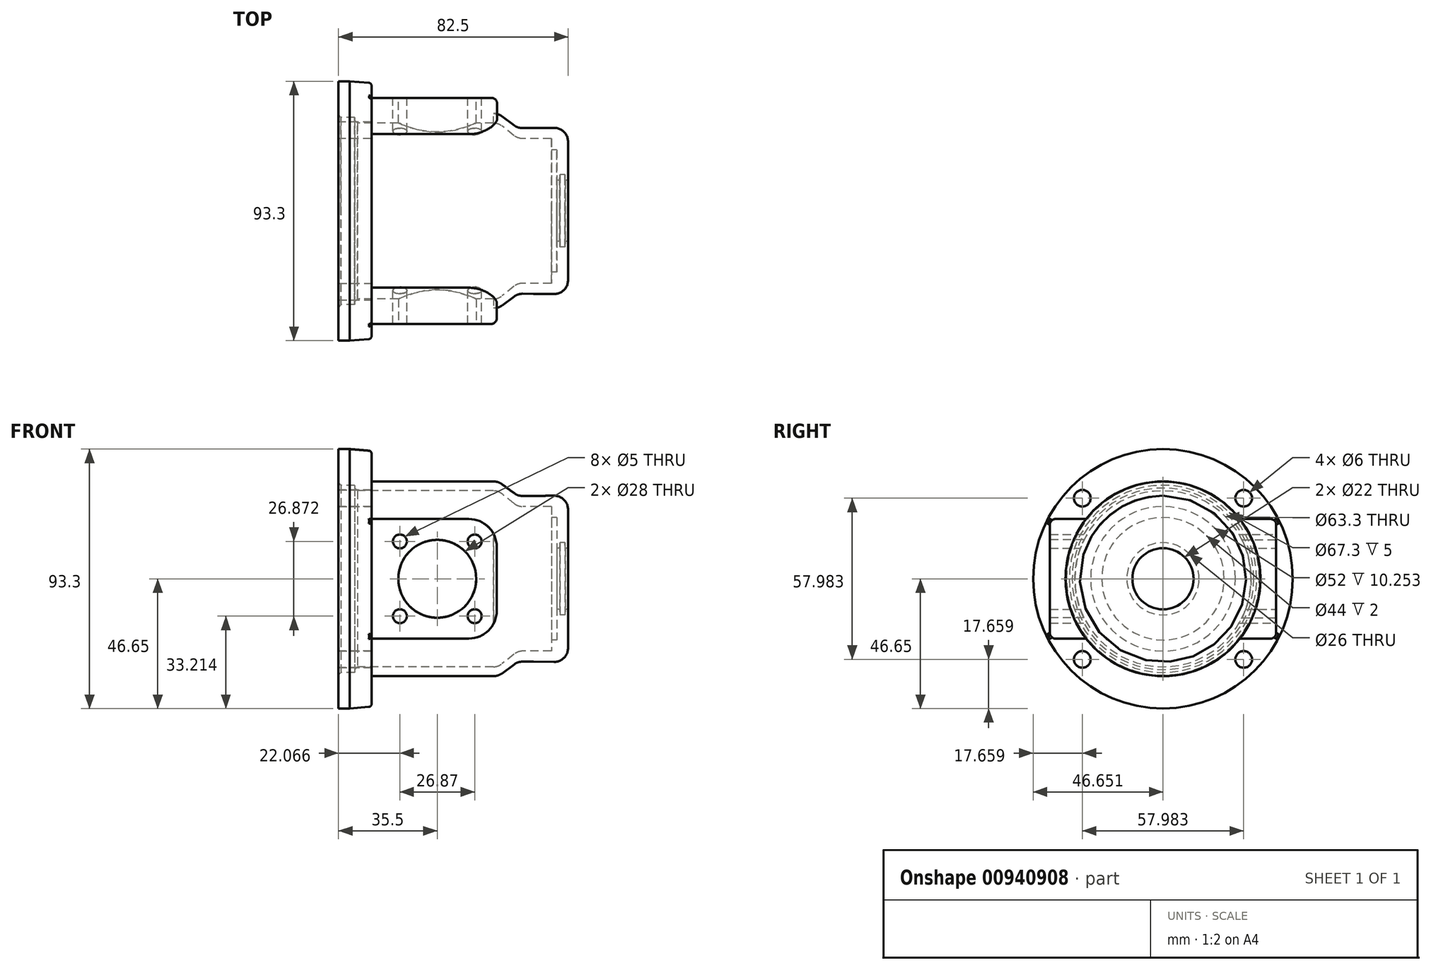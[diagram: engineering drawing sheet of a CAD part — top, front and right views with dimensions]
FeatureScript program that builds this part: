
annotation { "Feature Type Name" : "Feature", "Feature Type Description" : "" }
export const myFeature = defineFeature(function(context is Context, id is Id, definition is map)
    precondition{}
    {
        {
            var Q0;
            Q0=qCreatedBy(makeId("Front.planeOp"),FACE);
            var sketch = newSketch(context, id + "F0", { "sketchPlane" : qUnion([Q0])});
            skLineSegment(sketch, "E0", {"start": v(-19.49, 34.65) * mm, "end": v(-19.49, 46.65) * mm});
            skLineSegment(sketch, "E1", {"start": v(-19.49, 46.65) * mm, "end": v(-15.49, 46.65) * mm});
            skLineSegment(sketch, "E2", {"start": v(-7.63, 46) * mm, "end": v(-15.49, 46.65) * mm});
            skLineSegment(sketch, "E3", {"start": v(-7.63, 46) * mm, "end": v(-7.63, 35) * mm});
            skLineSegment(sketch, "E4", {"start": v(-18.63, 33.65) * mm, "end": v(-19.49, 34.65) * mm});
            skLineSegment(sketch, "E5", {"start": v(-18.63, 33.65) * mm, "end": v(-13.63, 33.65) * mm});
            skLineSegment(sketch, "E6", {"start": v(-13.63, 33.65) * mm, "end": v(-13.63, 32.65) * mm});
            skLineSegment(sketch, "E7", {"start": v(-12.63, 31.65) * mm, "end": v(-13.63, 32.65) * mm});
            skLineSegment(sketch, "E8", {"start": v(0, 0) * mm, "end": v(36.35, 0) * mm});
            skLineSegment(sketch, "E9", {"start": v(57.01, 26) * mm, "end": v(57.01, 22) * mm});
            skPoint(sketch, "E10.newPointB", {"position": v(45.67, 29.78) * mm});
            skPoint(sketch, "E11.orphan", {"position": v(61.56, 0) * mm});
            skLineSegment(sketch, "E12", {"start": v(63.01, 29.93) * mm, "end": v(63.01, 22) * mm});
            skLineSegment(sketch, "E13", {"start": v(13.91, 31.65) * mm, "end": v(33.91, 31.65) * mm});
            skLineSegment(sketch, "E14", {"start": v(-1.09, 35) * mm, "end": v(13.91, 35) * mm});
            skLineSegment(sketch, "E15", {"start": v(-6.09, 31.65) * mm, "end": v(13.91, 31.65) * mm});
            skLineSegment(sketch, "E16", {"start": v(33.91, 31.65) * mm, "end": v(36.17, 31.65) * mm});
            skLineSegment(sketch, "E17", {"start": v(48.77, 26) * mm, "end": v(57.01, 26) * mm});
            skLineSegment(sketch, "E18", {"start": v(50.6, 29.82) * mm, "end": v(63.01, 29.93) * mm});
            skLineSegment(sketch, "E19", {"start": v(-7.63, 35) * mm, "end": v(-1.09, 35) * mm});
            skLineSegment(sketch, "E20", {"start": v(-6.09, 31.65) * mm, "end": v(-12.63, 31.65) * mm});
            skLineSegment(sketch, "E21", {"start": v(46.76, 26) * mm, "end": v(48.77, 26) * mm});
            skLineSegment(sketch, "E22", {"start": v(39.28, 30.56) * mm, "end": v(43.65, 27.09) * mm});
            skPoint(sketch, "E23.visualSharp", {"position": v(37.91, 31.65) * mm});
            skArc(sketch, "E23.filletArc", {"start": v(39.28, 30.56) * mm, "mid": v(37.82, 31.37) * mm, "end": v(36.17, 31.65) * mm});
            skLineSegment(sketch, "E24", {"start": v(50.6, 29.82) * mm, "end": v(46.67, 29.8) * mm});
            skLineSegment(sketch, "E25", {"start": v(43.68, 30.76) * mm, "end": v(39.24, 34.03) * mm});
            skLineSegment(sketch, "E26", {"start": v(13.91, 35) * mm, "end": v(36.28, 35) * mm});
            skPoint(sketch, "E27.visualSharp", {"position": v(37.91, 35) * mm});
            skPoint(sketch, "E28.visualSharp", {"position": v(45.01, 29.78) * mm});
            skArc(sketch, "E28.filletArc", {"start": v(43.68, 30.76) * mm, "mid": v(45.1, 30.04) * mm, "end": v(46.67, 29.8) * mm});
            skArc(sketch, "E29.filletArc", {"start": v(39.24, 34.03) * mm, "mid": v(37.83, 34.75) * mm, "end": v(36.28, 35) * mm});
            skPoint(sketch, "E30.visualSharp", {"position": v(45.01, 26) * mm});
            skArc(sketch, "E30.filletArc", {"start": v(43.65, 27.09) * mm, "mid": v(45.11, 26.28) * mm, "end": v(46.76, 26) * mm});
            skLineSegment(sketch, "E31", {"start": v(63.01, 11) * mm, "end": v(62.51, 11) * mm});
            skLineSegment(sketch, "E32", {"start": v(63.01, 11) * mm, "end": v(63.01, 22) * mm});
            skPoint(sketch, "E33.start.orphan", {"position": v(63.01, 0) * mm});
            skLineSegment(sketch, "E34", {"start": v(57.01, 22) * mm, "end": v(59.01, 22) * mm});
            skLineSegment(sketch, "E35", {"start": v(59.01, 22) * mm, "end": v(59.01, 11) * mm});
            skPoint(sketch, "E36.orphan", {"position": v(57.01, 11) * mm});
            skLineSegment(sketch, "E37", {"start": v(59.01, 11) * mm, "end": v(59.51, 11) * mm});
            skPoint(sketch, "E38.endSnap0", {"position": v(61.01, 11) * mm});
            skLineSegment(sketch, "E39.trimOffspring", {"start": v(59.51, 11) * mm, "end": v(59.01, 11) * mm});
            skLineSegment(sketch, "E40", {"start": v(60.01, 11) * mm, "end": v(59.51, 11) * mm});
            skLineSegment(sketch, "E41", {"start": v(62.01, 11) * mm, "end": v(62.51, 11) * mm});
            skLineSegment(sketch, "E42", {"start": v(60.15, 13) * mm, "end": v(60.01, 11) * mm});
            skLineSegment(sketch, "E43", {"start": v(61.88, 13) * mm, "end": v(62.01, 11) * mm});
            skLineSegment(sketch, "E44", {"start": v(61.01, 11) * mm, "end": v(61.01, 13) * mm});
            skLineSegment(sketch, "E45", {"start": v(61.01, 13) * mm, "end": v(61.88, 13) * mm});
            skLineSegment(sketch, "E46", {"start": v(61.88, 13) * mm, "end": v(60.15, 13) * mm});
            skPoint(sketch, "E47.start.orphan", {"position": v(61.01, 14) * mm});
            skSolve(sketch);
        }
        {
            var Q0;
            Q0=makeQuery(id+"F0.imprint","IMPRINT",FACE,{"disambiguationData":[TD([[makeQuery(id+"F0.imprint","IMPRINT",EDGE,{"derivedFrom":sQuery(id+"F0.wireOp",EDGE,"E0")}),-1.0]])]});
            var Q1;
            Q1=sQuery(id+"F0.wireOp",EDGE,"E8");
            revolve(context, id + "F1", {"surfaceOperationType" : NewSurfaceOperationType.NEW, "entities" : qUnion([Q0]), "axis" : qUnion([Q1]), "revolveType" : RevolveType.FULL});
        }
        {
            var Q0;
            Q0=makeQuery(id+"F1.opRevolve","SWEPT_FACE",FACE,{"disambiguationData":[OSD([sQuery(id+"F0.wireOp",EDGE,"E0")])]});
            var sketch = newSketch(context, id + "F2", { "sketchPlane" : qUnion([Q0])});
            skCircle(sketch, "E48", {"center": v(29, 29) * mm, "radius": 3 * mm});
            skCircle(sketch, "E49", {"center": v(29, -29) * mm, "radius": 3 * mm});
            skCircle(sketch, "E50", {"center": v(-29, 29) * mm, "radius": 3 * mm});
            skCircle(sketch, "E51", {"center": v(-29, -29) * mm, "radius": 3 * mm});
            skSolve(sketch);
        }
        {
            var Q0;
            Q0 = qSketchRegion(id + "F2", true);
            extrude(context, id + "F3", {"entities" : qUnion([Q0]), "operationType" : NewBodyOperationType.REMOVE, "oppositeDirection" : true, "depth" : 18 * mm, "offsetDistance" : 25 * mm});
        }
        {
            var Q0;
            Q0=qCreatedBy(makeId("Front.planeOp"),FACE);
            var sketch = newSketch(context, id + "F4", { "sketchPlane" : qUnion([Q0])});
            skLineSegment(sketch, "E52.bottom", {"start": v(-40.89, 51.65) * mm, "end": v(82.62, 51.65) * mm});
            skLineSegment(sketch, "E52.top", {"start": v(-40.89, -57.32) * mm, "end": v(82.62, -57.32) * mm});
            skLineSegment(sketch, "E52.left", {"start": v(-40.89, 51.65) * mm, "end": v(-40.89, -57.32) * mm});
            skLineSegment(sketch, "E52.right", {"start": v(82.62, 51.65) * mm, "end": v(82.62, -57.32) * mm});
            skSolve(sketch);
        }
        {
            var Q0;
            Q0 = qSketchRegion(id + "F4", true);
            extrude(context, id + "F5", {"entities" : qUnion([Q0]), "operationType" : NewBodyOperationType.REMOVE, "depth" : 50 * mm, "offsetDistance" : 25 * mm});
        }
        {
            var Q0;
            Q0=makeQuery(id+"F1.opRevolve","SWEPT_FACE",FACE,{"disambiguationData":[OSD([sQuery(id+"F0.wireOp",EDGE,"E3")])]});
            var sketch = newSketch(context, id + "F6", { "sketchPlane" : qUnion([Q0])});
            skLineSegment(sketch, "E53", {"start": v(27.62, 21.5) * mm, "end": v(40.67, 21.5) * mm});
            skLineSegment(sketch, "E54", {"start": v(40.67, -21.5) * mm, "end": v(27.62, -21.5) * mm});
            skArc(sketch, "E55", {"start": v(27.62, -21.5) * mm, "mid": v(35, 0) * mm, "end": v(27.62, 21.5) * mm});
            skLineSegment(sketch, "E56", {"start": v(40.67, -21.5) * mm, "end": v(40.67, 21.5) * mm});
            skSolve(sketch);
        }
        {
            var Q0;
            Q0 = qSketchRegion(id + "F6", true);
            extrude(context, id + "F7", {"entities" : qUnion([Q0]), "operationType" : NewBodyOperationType.ADD, "depth" : 45.14 * mm, "offsetDistance" : 25 * mm});
        }
        {
            var Q0;
            Q0=makeQuery(id+"F1.opRevolve","SWEPT_EDGE",EDGE,{"disambiguationData":[OSD([sQuery(id+"F0.wireOp",EDGE,"E0"),sQuery(id+"F0.wireOp",EDGE,"E1")])]});
            cPoint(context, id + "F8", {"entities" : qUnion([Q0]), "parameter" : 0.5});
        }
        {
            var Q0;
            Q0=makeQuery(id+"F1.opRevolve","SWEPT_BODY",BODY,{"disambiguationData":[OSD([sQuery(id+"F0.wireOp",EDGE,"E0"),sQuery(id+"F0.wireOp",EDGE,"E1"),sQuery(id+"F0.wireOp",EDGE,"E2"),sQuery(id+"F0.wireOp",EDGE,"E3"),sQuery(id+"F0.wireOp",EDGE,"E4"),sQuery(id+"F0.wireOp",EDGE,"E5"),sQuery(id+"F0.wireOp",EDGE,"E6"),sQuery(id+"F0.wireOp",EDGE,"E7"),sQuery(id+"F0.wireOp",EDGE,"E9"),sQuery(id+"F0.wireOp",EDGE,"ttlMiW8K-Gj9s-mpOc-sAAF-bqFsmYQRB0dC"),sQuery(id+"F0.wireOp",EDGE,"dxv8NDji-zJk3-8ekn-KFhB-3ztd8SCryWd5"),sQuery(id+"F0.wireOp",EDGE,"E10.filletArc"),sQuery(id+"F0.wireOp",EDGE,"ruUsSjiC-r07a-THA8-P1NI-kNvXG15OnYoc"),sQuery(id+"F0.wireOp",EDGE,"abe5eb92-0ac8-4b74-8677-3c686329f105.filletArc"),sQuery(id+"F0.wireOp",EDGE,"h7bsjftr-fzGa-4ARr-nZfh-VTAOwtfqHb7T"),sQuery(id+"F0.wireOp",EDGE,"3mzqurQ0-g41q-c2LK-6E9X-WYiRKidhnamJ"),sQuery(id+"F0.wireOp",EDGE,"E12"),sQuery(id+"F0.wireOp",EDGE,"bZ8bIDva-nSo4-pdI0-vQef-kBVdg5MjayZi"),sQuery(id+"F0.wireOp",EDGE,"E13"),sQuery(id+"F0.wireOp",EDGE,"sj1dmuSO-go3f-yCpV-ps0s-w3yi9DrHe0LX"),sQuery(id+"F0.wireOp",EDGE,"h7XH48Ex-fpgu-Afb6-qUXn-9KPbAsaJLCzl")])]});
            var Q1;
            Q1 = qCreatedBy(id + "F8" ,VERTEX);
            var Q2;
            Q2=qCreatedBy(makeId("Origin.pointOp"),VERTEX);
            transform(context, id + "F9", {"entities" : qUnion([Q0]), "transformType" : TransformType.TRANSLATION_ENTITY, "oppositeDirectionEntity" : false, "transformLine" : qUnion([Q1, Q2]), "makeCopy" : false});
        }
        {
            var Q0;
            Q0=qCreatedBy(makeId("Front.planeOp"),FACE);
            var sketch = newSketch(context, id + "F10", { "sketchPlane" : qUnion([Q0])});
            skCircle(sketch, "E57", {"center": v(35.5, 0) * mm, "radius": 14 * mm});
            skSolve(sketch);
        }
        {
            var Q0;
            Q0 = qSketchRegion(id + "F10", true);
            extrude(context, id + "F11", {"entities" : qUnion([Q0]), "operationType" : NewBodyOperationType.REMOVE, "depth" : 25 * mm, "offsetDistance" : 25 * mm});
        }
        {
            var Q0;
            Q0=makeQuery(id+"F7.opExtrude","CAP_EDGE",EDGE,{"disambiguationData":[OSD([sQuery(id+"F6.wireOp",EDGE,"E54")])],"isStart":false});
            var Q1;
            Q1=makeQuery(id+"F7.opExtrude","CAP_EDGE",EDGE,{"disambiguationData":[OSD([sQuery(id+"F6.wireOp",EDGE,"E53")])],"isStart":false});
            fillet(context, id + "F12", {"entities" : qUnion([Q0, Q1]), "radius" : 10 * mm, "tangentPropagation" : true, "allowEdgeOverflow" : false});
        }
        {
            var Q0;
            Q0=makeQuery(id+"F7.opExtrude","SWEPT_EDGE",EDGE,{"disambiguationData":[OSD([sQuery(id+"F0.wireOp",EDGE,"E2"),sQuery(id+"F0.wireOp",EDGE,"E3"),sQuery(id+"F6.wireOp",EDGE,"E53"),sQuery(id+"F6.wireOp",EDGE,"E56")])]});
            fillet(context, id + "F13", {"entities" : qUnion([Q0]), "radius" : 2 * mm, "tangentPropagation" : true, "allowEdgeOverflow" : false});
        }
        {
            var Q0;
            Q0=makeQuery(id+"F1.opRevolve","SWEPT_EDGE",EDGE,{"disambiguationData":[OSD([sQuery(id+"F0.wireOp",EDGE,"E12"),sQuery(id+"F0.wireOp",EDGE,"E18")])]});
            fillet(context, id + "F14", {"entities" : qUnion([Q0]), "radius" : 5 * mm, "tangentPropagation" : true, "allowEdgeOverflow" : false});
        }
        {
            var Q0;
            {var subQ0=sQuery(id+"F0.wireOp",EDGE,"E3");var subQ1=sQuery(id+"F0.wireOp",EDGE,"E2");Q0=makeQuery(id+"F7.boolean.opBoolean","SPLIT",EDGE,{"disambiguationData":[TD([makeQuery(id+"F1.opRevolve","SWEPT_FACE",FACE,{"disambiguationData":[OSD([subQ1])]}),makeQuery(id+"F1.opRevolve","SWEPT_FACE",FACE,{"disambiguationData":[OSD([subQ0])]}),makeQuery(id+"F5.boolean.opBoolean","COPY",FACE,{"disambiguationData":[OD(0.0)],"derivedFrom":makeQuery(id+"F5.opExtrude","CAP_FACE",FACE,{"disambiguationData":[OSD([sQuery(id+"F4.wireOp",EDGE,"E52.bottom"),sQuery(id+"F4.wireOp",EDGE,"E52.top"),sQuery(id+"F4.wireOp",EDGE,"E52.left"),sQuery(id+"F4.wireOp",EDGE,"E52.right")])],"isStart":true})}),makeQuery(id+"F7.opExtrude","SWEPT_FACE",FACE,{"disambiguationData":[OSD([sQuery(id+"F6.wireOp",EDGE,"E54")])]}),makeQuery(id+"F7.opExtrude","SWEPT_FACE",FACE,{"disambiguationData":[OSD([sQuery(id+"F6.wireOp",EDGE,"E56")])]})])],"derivedFrom":makeQuery(id+"F1.opRevolve","SWEPT_EDGE",EDGE,{"disambiguationData":[OSD([subQ1,subQ0])]})});}
            var Q1;
            {var subQ0=sQuery(id+"F0.wireOp",EDGE,"E3");var subQ1=sQuery(id+"F0.wireOp",EDGE,"E2");Q1=makeQuery(id+"F7.boolean.opBoolean","SPLIT",EDGE,{"disambiguationData":[TD([makeQuery(id+"F1.opRevolve","SWEPT_FACE",FACE,{"disambiguationData":[OSD([subQ1])]}),makeQuery(id+"F1.opRevolve","SWEPT_FACE",FACE,{"disambiguationData":[OSD([subQ0])]}),makeQuery(id+"F7.opExtrude","SWEPT_FACE",FACE,{"disambiguationData":[OSD([sQuery(id+"F6.wireOp",EDGE,"E53")])]}),makeQuery(id+"F7.opExtrude","SWEPT_FACE",FACE,{"disambiguationData":[OSD([sQuery(id+"F6.wireOp",EDGE,"E54")])]}),makeQuery(id+"F7.opExtrude","SWEPT_FACE",FACE,{"disambiguationData":[OSD([sQuery(id+"F6.wireOp",EDGE,"E56")])]})])],"derivedFrom":makeQuery(id+"F1.opRevolve","SWEPT_EDGE",EDGE,{"disambiguationData":[OSD([subQ1,subQ0])]})});}
            var Q2;
            {var subQ0=sQuery(id+"F0.wireOp",EDGE,"E3");var subQ1=sQuery(id+"F0.wireOp",EDGE,"E2");Q2=makeQuery(id+"F7.boolean.opBoolean","SPLIT",EDGE,{"disambiguationData":[TD([makeQuery(id+"F1.opRevolve","SWEPT_FACE",FACE,{"disambiguationData":[OSD([subQ1])]}),makeQuery(id+"F1.opRevolve","SWEPT_FACE",FACE,{"disambiguationData":[OSD([subQ0])]}),makeQuery(id+"F5.boolean.opBoolean","COPY",FACE,{"disambiguationData":[OD(1.0)],"derivedFrom":makeQuery(id+"F5.opExtrude","CAP_FACE",FACE,{"disambiguationData":[OSD([sQuery(id+"F4.wireOp",EDGE,"E52.bottom"),sQuery(id+"F4.wireOp",EDGE,"E52.top"),sQuery(id+"F4.wireOp",EDGE,"E52.left"),sQuery(id+"F4.wireOp",EDGE,"E52.right")])],"isStart":true})}),makeQuery(id+"F7.opExtrude","SWEPT_FACE",FACE,{"disambiguationData":[OSD([sQuery(id+"F6.wireOp",EDGE,"E53")])]}),makeQuery(id+"F7.opExtrude","SWEPT_FACE",FACE,{"disambiguationData":[OSD([sQuery(id+"F6.wireOp",EDGE,"E56")])]})])],"derivedFrom":makeQuery(id+"F1.opRevolve","SWEPT_EDGE",EDGE,{"disambiguationData":[OSD([subQ1,subQ0])]})});}
            fillet(context, id + "F15", {"entities" : qUnion([Q0, Q1, Q2]), "radius" : 1 * mm, "tangentPropagation" : true, "allowEdgeOverflow" : false});
        }
        {
            var Q0;
            Q0=makeQuery(id+"F5.boolean.opBoolean","COPY",FACE,{"disambiguationData":[OD(1.0)],"derivedFrom":makeQuery(id+"F5.opExtrude","CAP_FACE",FACE,{"disambiguationData":[OSD([sQuery(id+"F4.wireOp",EDGE,"E52.bottom"),sQuery(id+"F4.wireOp",EDGE,"E52.top"),sQuery(id+"F4.wireOp",EDGE,"E52.left"),sQuery(id+"F4.wireOp",EDGE,"E52.right")])],"isStart":true})});
            var sketch = newSketch(context, id + "F16", { "sketchPlane" : qUnion([Q0])});
            skLineSegment(sketch, "E58", {"start": v(0, 34.65) * mm, "end": v(0, 46.65) * mm});
            skLineSegment(sketch, "E59", {"start": v(0, 46.65) * mm, "end": v(4, 46.65) * mm});
            skLineSegment(sketch, "E60", {"start": v(11.86, 46) * mm, "end": v(4, 46.65) * mm});
            skLineSegment(sketch, "E61", {"start": v(11.86, 46) * mm, "end": v(11.86, 35) * mm});
            skLineSegment(sketch, "E62", {"start": v(0.86, 33.65) * mm, "end": v(0, 34.65) * mm});
            skLineSegment(sketch, "E63", {"start": v(0.86, 33.65) * mm, "end": v(5.86, 33.65) * mm});
            skLineSegment(sketch, "E64", {"start": v(5.86, 33.65) * mm, "end": v(5.86, 32.65) * mm});
            skLineSegment(sketch, "E65", {"start": v(6.86, 31.65) * mm, "end": v(5.86, 32.65) * mm});
            skLineSegment(sketch, "E66", {"start": v(0, 0) * mm, "end": v(36.35, 0) * mm});
            skLineSegment(sketch, "E67", {"start": v(76.5, 26) * mm, "end": v(76.5, 22) * mm});
            skPoint(sketch, "E68.newPointB", {"position": v(65.15, 29.78) * mm});
            skPoint(sketch, "E69.orphan", {"position": v(81.05, 0) * mm});
            skLineSegment(sketch, "E70", {"start": v(82.5, 29.93) * mm, "end": v(82.5, 22) * mm});
            skLineSegment(sketch, "E71", {"start": v(33.4, 31.65) * mm, "end": v(53.4, 31.65) * mm});
            skLineSegment(sketch, "E72", {"start": v(18.4, 35) * mm, "end": v(33.4, 35) * mm});
            skLineSegment(sketch, "E73", {"start": v(13.4, 31.65) * mm, "end": v(33.4, 31.65) * mm});
            skLineSegment(sketch, "E74", {"start": v(53.4, 31.65) * mm, "end": v(55.66, 31.65) * mm});
            skLineSegment(sketch, "E75", {"start": v(68.26, 26) * mm, "end": v(76.5, 26) * mm});
            skLineSegment(sketch, "E76", {"start": v(70.09, 29.82) * mm, "end": v(82.5, 29.93) * mm});
            skLineSegment(sketch, "E77", {"start": v(11.86, 35) * mm, "end": v(18.4, 35) * mm});
            skLineSegment(sketch, "E78", {"start": v(13.4, 31.65) * mm, "end": v(6.86, 31.65) * mm});
            skLineSegment(sketch, "E79", {"start": v(66.25, 26) * mm, "end": v(68.26, 26) * mm});
            skLineSegment(sketch, "E80", {"start": v(58.77, 30.56) * mm, "end": v(63.13, 27.09) * mm});
            skPoint(sketch, "E81.visualSharp", {"position": v(57.4, 31.65) * mm});
            skArc(sketch, "E81.filletArc", {"start": v(58.77, 30.56) * mm, "mid": v(57.3, 31.37) * mm, "end": v(55.66, 31.65) * mm});
            skLineSegment(sketch, "E82", {"start": v(70.09, 29.82) * mm, "end": v(66.16, 29.8) * mm});
            skLineSegment(sketch, "E83", {"start": v(63.17, 30.76) * mm, "end": v(58.72, 34.03) * mm});
            skLineSegment(sketch, "E84", {"start": v(33.4, 35) * mm, "end": v(55.76, 35) * mm});
            skPoint(sketch, "E85.visualSharp", {"position": v(57.4, 35) * mm});
            skPoint(sketch, "E86.visualSharp", {"position": v(64.5, 29.78) * mm});
            skArc(sketch, "E86.filletArc", {"start": v(63.17, 30.76) * mm, "mid": v(64.58, 30.04) * mm, "end": v(66.16, 29.8) * mm});
            skArc(sketch, "E87.filletArc", {"start": v(58.72, 34.03) * mm, "mid": v(57.32, 34.75) * mm, "end": v(55.76, 35) * mm});
            skPoint(sketch, "E88.visualSharp", {"position": v(64.5, 26) * mm});
            skArc(sketch, "E88.filletArc", {"start": v(63.13, 27.09) * mm, "mid": v(64.6, 26.28) * mm, "end": v(66.25, 26) * mm});
            skLineSegment(sketch, "E89", {"start": v(82.5, 11) * mm, "end": v(82, 11) * mm});
            skLineSegment(sketch, "E90", {"start": v(82.5, 11) * mm, "end": v(82.5, 22) * mm});
            skPoint(sketch, "E91.start.orphan", {"position": v(82.5, 0) * mm});
            skLineSegment(sketch, "E92", {"start": v(76.5, 22) * mm, "end": v(78.5, 22) * mm});
            skLineSegment(sketch, "E93", {"start": v(78.5, 22) * mm, "end": v(78.5, 11) * mm});
            skPoint(sketch, "E94.orphan", {"position": v(76.5, 11) * mm});
            skLineSegment(sketch, "E95", {"start": v(78.5, 11) * mm, "end": v(79, 11) * mm});
            skPoint(sketch, "E96.endSnap0", {"position": v(80.5, 11) * mm});
            skLineSegment(sketch, "E97.trimOffspring", {"start": v(79, 11) * mm, "end": v(78.5, 11) * mm});
            skLineSegment(sketch, "E98", {"start": v(79.5, 11) * mm, "end": v(79, 11) * mm});
            skLineSegment(sketch, "E99", {"start": v(81.5, 11) * mm, "end": v(82, 11) * mm});
            skLineSegment(sketch, "E100", {"start": v(79.63, 13) * mm, "end": v(79.5, 11) * mm});
            skLineSegment(sketch, "E101", {"start": v(81.37, 13) * mm, "end": v(81.5, 11) * mm});
            skLineSegment(sketch, "E102", {"start": v(80.5, 11) * mm, "end": v(80.5, 13) * mm});
            skLineSegment(sketch, "E103", {"start": v(80.5, 13) * mm, "end": v(81.37, 13) * mm});
            skLineSegment(sketch, "E104", {"start": v(81.37, 13) * mm, "end": v(79.63, 13) * mm});
            skPoint(sketch, "E105.start.orphan", {"position": v(80.5, 14) * mm});
            skSolve(sketch);
        }
        {
            var Q0;
            Q0 = qSketchRegion(id + "F16", true);
            var Q1;
            Q1=sQuery(id+"F16.wireOp",EDGE,"E66");
            revolve(context, id + "F17", {"operationType" : NewBodyOperationType.ADD, "surfaceOperationType" : NewSurfaceOperationType.NEW, "entities" : qUnion([Q0]), "axis" : qUnion([Q1]), "revolveType" : RevolveType.ONE_DIRECTION, "angle" : 180 * degree});
        }
        {
            var Q0;
            Q0=makeQuery(id+"F17.opRevolve","SWEPT_EDGE",EDGE,{"disambiguationData":[OSD([sQuery(id+"F16.wireOp",EDGE,"E70"),sQuery(id+"F16.wireOp",EDGE,"E76")])]});
            fillet(context, id + "F18", {"entities" : qUnion([Q0]), "radius" : 5 * mm, "tangentPropagation" : true, "allowEdgeOverflow" : false});
        }
        {
            var Q0;
            {var subQ0=makeQuery(id+"F1.opRevolve","SWEPT_FACE",FACE,{"disambiguationData":[OSD([sQuery(id+"F0.wireOp",EDGE,"E14"),sQuery(id+"F0.wireOp",EDGE,"E19"),sQuery(id+"F0.wireOp",EDGE,"E26")])]});var subQ1=makeQuery(id+"F1.opRevolve","SWEPT_FACE",FACE,{"disambiguationData":[OSD([sQuery(id+"F0.wireOp",EDGE,"E3")])]});var subQ2=makeQuery(id+"F7.opExtrude","SWEPT_FACE",FACE,{"disambiguationData":[OSD([sQuery(id+"F6.wireOp",EDGE,"E54")])]});var subQ3=makeQuery(id+"F1.opRevolve","SWEPT_FACE",FACE,{"disambiguationData":[OSD([sQuery(id+"F0.wireOp",EDGE,"E2")])]});var subQ4=makeQuery(id+"F5.opExtrude","CAP_FACE",FACE,{"disambiguationData":[OSD([sQuery(id+"F4.wireOp",EDGE,"E52.bottom"),sQuery(id+"F4.wireOp",EDGE,"E52.top"),sQuery(id+"F4.wireOp",EDGE,"E52.left"),sQuery(id+"F4.wireOp",EDGE,"E52.right")])],"isStart":true});var subQ5=makeQuery(id+"F7.opExtrude","SWEPT_FACE",FACE,{"disambiguationData":[OSD([sQuery(id+"F6.wireOp",EDGE,"E56")])]});var subQ6=subQ1;var subQ7=makeQuery(id+"F7.opExtrude","SWEPT_FACE",FACE,{"disambiguationData":[OSD([sQuery(id+"F6.wireOp",EDGE,"E53")])]});var subQ8=makeQuery(id+"F13.opFillet","MERGE",FACE,{"derivedFrom":[makeQuery(id+"F7.boolean.opBoolean","SPLIT",FACE,{"disambiguationData":[TD([subQ3,subQ1,subQ7,subQ2,subQ5])],"derivedFrom":subQ6}),makeQuery(id+"F7.boolean.opBoolean","SPLIT",FACE,{"disambiguationData":[TD([subQ3,subQ1,subQ0,makeQuery(id+"F3.boolean.opBoolean","COPY",FACE,{"derivedFrom":makeQuery(id+"F3.opExtrude","SWEPT_FACE",FACE,{"disambiguationData":[OSD([sQuery(id+"F2.wireOp",EDGE,"E50")])]})}),makeQuery(id+"F5.boolean.opBoolean","COPY",FACE,{"disambiguationData":[OD(1.0)],"derivedFrom":subQ4}),subQ7,subQ5])],"derivedFrom":subQ6}),makeQuery(id+"F7.boolean.opBoolean","SPLIT",FACE,{"disambiguationData":[TD([subQ3,subQ1,subQ0,makeQuery(id+"F3.boolean.opBoolean","COPY",FACE,{"derivedFrom":makeQuery(id+"F3.opExtrude","SWEPT_FACE",FACE,{"disambiguationData":[OSD([sQuery(id+"F2.wireOp",EDGE,"E51")])]})}),makeQuery(id+"F5.boolean.opBoolean","COPY",FACE,{"disambiguationData":[OD(0.0)],"derivedFrom":subQ4}),subQ2,subQ5])],"derivedFrom":subQ6})]});Q0=makeQuery(id+"F17.boolean.opBoolean","MERGE",FACE,{"derivedFrom":[makeQuery(id+"F15.opFillet","SPLIT",FACE,{"disambiguationData":[OD(0.0)],"derivedFrom":subQ8}),makeQuery(id+"F15.opFillet","SPLIT",FACE,{"disambiguationData":[OD(1.0)],"derivedFrom":subQ8}),makeQuery(id+"F17.opRevolve","SWEPT_FACE",FACE,{"disambiguationData":[OSD([sQuery(id+"F16.wireOp",EDGE,"E61")])]})]});}
            var sketch = newSketch(context, id + "F19", { "sketchPlane" : qUnion([Q0])});
            skLineSegment(sketch, "E106.MirrorCS", {"start": v(-87.32, -21.5) * mm, "end": v(-74.27, -21.5) * mm});
            skLineSegment(sketch, "E107.MirrorCS", {"start": v(-87.32, -21.5) * mm, "end": v(-87.32, 21.5) * mm});
            skLineSegment(sketch, "E108.MirrorCS", {"start": v(-74.27, 21.5) * mm, "end": v(-87.32, 21.5) * mm});
            skArc(sketch, "E109.MirrorCS", {"start": v(-74.27, -21.5) * mm, "mid": v(-81.65, 0) * mm, "end": v(-74.27, 21.5) * mm});
            skSolve(sketch);
        }
        {
            var Q0;
            {var subQ0=sQuery(id+"F19.wireOp",EDGE,"E109.MirrorCS");Q0=makeQuery(id+"F19.imprint","IMPRINT",FACE,{"disambiguationData":[TD([[makeQuery(id+"F19.imprint","IMPRINT",EDGE,{"derivedFrom":subQ0}),1.0]])]});}
            extrude(context, id + "F20", {"entities" : qUnion([Q0]), "operationType" : NewBodyOperationType.ADD, "depth" : 45 * mm, "offsetDistance" : 25 * mm});
        }
        {
            var Q0;
            Q0=makeQuery(id+"F20.opExtrude","CAP_EDGE",EDGE,{"disambiguationData":[OSD([sQuery(id+"F19.wireOp",EDGE,"E108.MirrorCS")])],"isStart":false});
            var Q1;
            Q1=makeQuery(id+"F20.opExtrude","CAP_EDGE",EDGE,{"disambiguationData":[OSD([sQuery(id+"F19.wireOp",EDGE,"E106.MirrorCS")])],"isStart":false});
            fillet(context, id + "F21", {"entities" : qUnion([Q0, Q1]), "radius" : 10 * mm, "tangentPropagation" : true, "allowEdgeOverflow" : false});
        }
        {
            var Q0;
            Q0=makeQuery(id+"F20.opExtrude","SWEPT_EDGE",EDGE,{"disambiguationData":[OSD([sQuery(id+"F16.wireOp",EDGE,"E60"),sQuery(id+"F16.wireOp",EDGE,"E61"),sQuery(id+"F19.wireOp",EDGE,"E106.MirrorCS"),sQuery(id+"F19.wireOp",EDGE,"E107.MirrorCS")])]});
            fillet(context, id + "F22", {"entities" : qUnion([Q0]), "radius" : 2 * mm, "tangentPropagation" : true, "allowEdgeOverflow" : false});
        }
        {
            var Q0;
            {var subQ0=sQuery(id+"F16.wireOp",EDGE,"E61");var subQ1=sQuery(id+"F16.wireOp",EDGE,"E60");Q0=makeQuery(id+"F20.boolean.opBoolean","SPLIT",EDGE,{"disambiguationData":[TD([makeQuery(id+"F1.opRevolve","SWEPT_FACE",FACE,{"disambiguationData":[OSD([sQuery(id+"F0.wireOp",EDGE,"E3")])]}),makeQuery(id+"F17.opRevolve","CAP_FACE",FACE,{"disambiguationData":[OSD([sQuery(id+"F16.wireOp",EDGE,"E58"),sQuery(id+"F16.wireOp",EDGE,"E59"),subQ1,subQ0,sQuery(id+"F16.wireOp",EDGE,"E62"),sQuery(id+"F16.wireOp",EDGE,"E63"),sQuery(id+"F16.wireOp",EDGE,"E64"),sQuery(id+"F16.wireOp",EDGE,"E65"),sQuery(id+"F16.wireOp",EDGE,"E67"),sQuery(id+"F16.wireOp",EDGE,"E70"),sQuery(id+"F16.wireOp",EDGE,"E71"),sQuery(id+"F16.wireOp",EDGE,"E72"),sQuery(id+"F16.wireOp",EDGE,"E73"),sQuery(id+"F16.wireOp",EDGE,"E74"),sQuery(id+"F16.wireOp",EDGE,"E75"),sQuery(id+"F16.wireOp",EDGE,"E76"),sQuery(id+"F16.wireOp",EDGE,"E77"),sQuery(id+"F16.wireOp",EDGE,"E78"),sQuery(id+"F16.wireOp",EDGE,"E79"),sQuery(id+"F16.wireOp",EDGE,"E80"),sQuery(id+"F16.wireOp",EDGE,"E81.filletArc"),sQuery(id+"F16.wireOp",EDGE,"E82"),sQuery(id+"F16.wireOp",EDGE,"E83"),sQuery(id+"F16.wireOp",EDGE,"E84"),sQuery(id+"F16.wireOp",EDGE,"E86.filletArc"),sQuery(id+"F16.wireOp",EDGE,"E87.filletArc"),sQuery(id+"F16.wireOp",EDGE,"E88.filletArc"),sQuery(id+"F16.wireOp",EDGE,"E89"),sQuery(id+"F16.wireOp",EDGE,"E90"),sQuery(id+"F16.wireOp",EDGE,"E92"),sQuery(id+"F16.wireOp",EDGE,"E93"),sQuery(id+"F16.wireOp",EDGE,"E97.trimOffspring"),sQuery(id+"F16.wireOp",EDGE,"E98"),sQuery(id+"F16.wireOp",EDGE,"E99"),sQuery(id+"F16.wireOp",EDGE,"E100"),sQuery(id+"F16.wireOp",EDGE,"E101"),sQuery(id+"F16.wireOp",EDGE,"E104")])],"isStart":true}),makeQuery(id+"F17.opRevolve","SWEPT_FACE",FACE,{"disambiguationData":[OSD([subQ1])]}),makeQuery(id+"F17.opRevolve","SWEPT_FACE",FACE,{"disambiguationData":[OSD([subQ0])]}),makeQuery(id+"F20.opExtrude","SWEPT_FACE",FACE,{"disambiguationData":[OSD([sQuery(id+"F19.wireOp",EDGE,"E107.MirrorCS")])]}),makeQuery(id+"F20.opExtrude","SWEPT_FACE",FACE,{"disambiguationData":[OSD([sQuery(id+"F19.wireOp",EDGE,"E108.MirrorCS")])]})])],"derivedFrom":makeQuery(id+"F17.opRevolve","SWEPT_EDGE",EDGE,{"disambiguationData":[OSD([subQ1,subQ0])]})});}
            fillet(context, id + "F23", {"entities" : qUnion([Q0]), "radius" : 1 * mm, "tangentPropagation" : true, "allowEdgeOverflow" : false});
        }
        {
            var Q0;
            Q0=makeQuery(id+"F20.opExtrude","SWEPT_FACE",FACE,{"disambiguationData":[OSD([sQuery(id+"F19.wireOp",EDGE,"E107.MirrorCS")])]});
            var sketch = newSketch(context, id + "F24", { "sketchPlane" : qUnion([Q0])});
            skPoint(sketch, "E110.endSnap0", {"position": v(11.86, 0) * mm});
            skCircle(sketch, "E111", {"center": v(35.5, 0) * mm, "radius": 14 * mm});
            skSolve(sketch);
        }
        {
            var Q0;
            Q0=makeQuery(id+"F24.imprint","IMPRINT",FACE,{"disambiguationData":[TD([[makeQuery(id+"F24.imprint","IMPRINT",EDGE,{"derivedFrom":sQuery(id+"F24.wireOp",EDGE,"E111")}),1.0]])]});
            extrude(context, id + "F25", {"entities" : qUnion([Q0]), "operationType" : NewBodyOperationType.REMOVE, "oppositeDirection" : true, "depth" : 25 * mm, "offsetDistance" : 25 * mm});
        }
        {
            var Q0;
            {var subQ0=sQuery(id+"F16.wireOp",EDGE,"E61");var subQ1=makeQuery(id+"F17.opRevolve","SWEPT_FACE",FACE,{"disambiguationData":[OSD([subQ0])]});var subQ2=sQuery(id+"F6.wireOp",EDGE,"E54");var subQ3=makeQuery(id+"F7.opExtrude","SWEPT_FACE",FACE,{"disambiguationData":[OSD([subQ2])]});var subQ4=sQuery(id+"F0.wireOp",EDGE,"E3");var subQ5=makeQuery(id+"F1.opRevolve","SWEPT_FACE",FACE,{"disambiguationData":[OSD([subQ4])]});var subQ6=makeQuery(id+"F5.opExtrude","CAP_FACE",FACE,{"disambiguationData":[OSD([sQuery(id+"F4.wireOp",EDGE,"E52.bottom"),sQuery(id+"F4.wireOp",EDGE,"E52.top"),sQuery(id+"F4.wireOp",EDGE,"E52.left"),sQuery(id+"F4.wireOp",EDGE,"E52.right")])],"isStart":true});var subQ7=makeQuery(id+"F5.boolean.opBoolean","COPY",FACE,{"disambiguationData":[OD(0.0)],"derivedFrom":subQ6});var subQ8=sQuery(id+"F6.wireOp",EDGE,"E56");var subQ9=makeQuery(id+"F7.opExtrude","SWEPT_FACE",FACE,{"disambiguationData":[OSD([subQ8])]});var subQ10=sQuery(id+"F0.wireOp",EDGE,"E2");var subQ11=makeQuery(id+"F1.opRevolve","SWEPT_FACE",FACE,{"disambiguationData":[OSD([subQ10])]});var subQ12=makeQuery(id+"F1.opRevolve","SWEPT_EDGE",EDGE,{"disambiguationData":[OSD([subQ10,subQ4])]});var subQ13=makeQuery(id+"F7.boolean.opBoolean","SPLIT",EDGE,{"disambiguationData":[TD([subQ11,subQ5,subQ7,subQ3,subQ9])],"derivedFrom":subQ12});var subQ14=sQuery(id+"F16.wireOp",EDGE,"E104");var subQ15=sQuery(id+"F16.wireOp",EDGE,"E101");var subQ16=sQuery(id+"F16.wireOp",EDGE,"E100");var subQ17=sQuery(id+"F16.wireOp",EDGE,"E99");var subQ18=sQuery(id+"F16.wireOp",EDGE,"E98");var subQ19=sQuery(id+"F16.wireOp",EDGE,"E97.trimOffspring");var subQ20=sQuery(id+"F16.wireOp",EDGE,"E93");var subQ21=sQuery(id+"F16.wireOp",EDGE,"E92");var subQ22=sQuery(id+"F16.wireOp",EDGE,"E90");var subQ23=sQuery(id+"F16.wireOp",EDGE,"E89");var subQ24=sQuery(id+"F16.wireOp",EDGE,"E88.filletArc");var subQ25=sQuery(id+"F16.wireOp",EDGE,"E87.filletArc");var subQ26=sQuery(id+"F16.wireOp",EDGE,"E86.filletArc");var subQ27=sQuery(id+"F16.wireOp",EDGE,"E84");var subQ28=sQuery(id+"F16.wireOp",EDGE,"E83");var subQ29=sQuery(id+"F16.wireOp",EDGE,"E82");var subQ30=sQuery(id+"F16.wireOp",EDGE,"E81.filletArc");var subQ31=sQuery(id+"F16.wireOp",EDGE,"E80");var subQ32=sQuery(id+"F16.wireOp",EDGE,"E79");var subQ33=sQuery(id+"F16.wireOp",EDGE,"E78");var subQ34=sQuery(id+"F16.wireOp",EDGE,"E77");var subQ35=sQuery(id+"F16.wireOp",EDGE,"E76");var subQ36=sQuery(id+"F16.wireOp",EDGE,"E75");var subQ37=sQuery(id+"F16.wireOp",EDGE,"E74");var subQ38=sQuery(id+"F16.wireOp",EDGE,"E73");var subQ39=sQuery(id+"F16.wireOp",EDGE,"E72");var subQ40=sQuery(id+"F16.wireOp",EDGE,"E71");var subQ41=sQuery(id+"F16.wireOp",EDGE,"E70");var subQ42=sQuery(id+"F16.wireOp",EDGE,"E67");var subQ43=sQuery(id+"F16.wireOp",EDGE,"E65");var subQ44=sQuery(id+"F16.wireOp",EDGE,"E64");var subQ45=sQuery(id+"F16.wireOp",EDGE,"E63");var subQ46=sQuery(id+"F16.wireOp",EDGE,"E62");var subQ47=sQuery(id+"F16.wireOp",EDGE,"E60");var subQ48=sQuery(id+"F16.wireOp",EDGE,"E59");var subQ49=sQuery(id+"F16.wireOp",EDGE,"E58");var subQ50=makeQuery(id+"F20.opExtrude","SWEPT_FACE",FACE,{"disambiguationData":[OSD([sQuery(id+"F19.wireOp",EDGE,"E107.MirrorCS")])]});var subQ51=makeQuery(id+"F17.opRevolve","SWEPT_FACE",FACE,{"disambiguationData":[OSD([subQ47])]});var subQ52=makeQuery(id+"F1.opRevolve","SWEPT_FACE",FACE,{"disambiguationData":[OSD([sQuery(id+"F0.wireOp",EDGE,"E14"),sQuery(id+"F0.wireOp",EDGE,"E19"),sQuery(id+"F0.wireOp",EDGE,"E26")])]});var subQ53=makeQuery(id+"F3.boolean.opBoolean","COPY",FACE,{"derivedFrom":makeQuery(id+"F3.opExtrude","SWEPT_FACE",FACE,{"disambiguationData":[OSD([sQuery(id+"F2.wireOp",EDGE,"E51")])]})});var subQ54=makeQuery(id+"F17.opRevolve","SWEPT_FACE",FACE,{"disambiguationData":[OSD([subQ39,subQ34,subQ27])]});var subQ55=makeQuery(id+"F20.opExtrude","SWEPT_FACE",FACE,{"disambiguationData":[OSD([sQuery(id+"F19.wireOp",EDGE,"E106.MirrorCS")])]});var subQ56=subQ5;var subQ57=makeQuery(id+"F3.boolean.opBoolean","COPY",FACE,{"derivedFrom":makeQuery(id+"F3.opExtrude","SWEPT_FACE",FACE,{"disambiguationData":[OSD([sQuery(id+"F2.wireOp",EDGE,"E50")])]})});var subQ58=sQuery(id+"F6.wireOp",EDGE,"E53");var subQ59=makeQuery(id+"F7.opExtrude","SWEPT_FACE",FACE,{"disambiguationData":[OSD([subQ58])]});var subQ60=makeQuery(id+"F5.boolean.opBoolean","COPY",FACE,{"disambiguationData":[OD(1.0)],"derivedFrom":subQ6});var subQ61=makeQuery(id+"F13.opFillet","MERGE",FACE,{"derivedFrom":[makeQuery(id+"F7.boolean.opBoolean","SPLIT",FACE,{"disambiguationData":[TD([subQ11,subQ5,subQ59,subQ3,subQ9])],"derivedFrom":subQ56}),makeQuery(id+"F7.boolean.opBoolean","SPLIT",FACE,{"disambiguationData":[TD([subQ11,subQ5,subQ52,subQ57,subQ60,subQ59,subQ9])],"derivedFrom":subQ56}),makeQuery(id+"F7.boolean.opBoolean","SPLIT",FACE,{"disambiguationData":[TD([subQ11,subQ5,subQ52,subQ53,subQ7,subQ3,subQ9])],"derivedFrom":subQ56})]});var subQ62=makeQuery(id+"F17.boolean.opBoolean","MERGE",FACE,{"derivedFrom":[makeQuery(id+"F15.opFillet","SPLIT",FACE,{"disambiguationData":[OD(0.0)],"derivedFrom":subQ61}),makeQuery(id+"F15.opFillet","SPLIT",FACE,{"disambiguationData":[OD(1.0)],"derivedFrom":subQ61}),subQ1]});var subQ63=makeQuery(id+"F20.opExtrude","SWEPT_FACE",FACE,{"disambiguationData":[OSD([sQuery(id+"F19.wireOp",EDGE,"E108.MirrorCS")])]});Q0=makeQuery(id+"F23.opFillet","SPLIT",FACE,{"disambiguationData":[OD(0.0)],"derivedFrom":makeQuery(id+"F22.opFillet","MERGE",FACE,{"derivedFrom":[makeQuery(id+"F20.boolean.opBoolean","SPLIT",FACE,{"disambiguationData":[TD([subQ5,subQ51,subQ1,subQ55,subQ50,subQ63])],"derivedFrom":subQ62}),makeQuery(id+"F20.boolean.opBoolean","SPLIT",FACE,{"disambiguationData":[TD([subQ5,subQ52,subQ57,subQ59,makeQuery(id+"F13.opFillet","BLEND_FACE",FACE,{"disambiguationData":[OSD([subQ10,subQ4,subQ58,subQ8])]}),makeQuery(id+"F15.opFillet","BLEND_FACE",FACE,{"disambiguationData":[OSD([subQ10,subQ4]),TDD([makeQuery(id+"F7.boolean.opBoolean","SPLIT",EDGE,{"disambiguationData":[TD([subQ11,subQ5,subQ60,subQ59,subQ9])],"derivedFrom":subQ12})])]}),makeQuery(id+"F15.opFillet","BLEND_FACE",FACE,{"disambiguationData":[OSD([subQ10,subQ4]),TDD([makeQuery(id+"F7.boolean.opBoolean","SPLIT",EDGE,{"disambiguationData":[TD([subQ11,subQ5,subQ59,subQ3,subQ9])],"derivedFrom":subQ12})]),OD(0.0)]}),makeQuery(id+"F17.opRevolve","CAP_FACE",FACE,{"disambiguationData":[OSD([subQ49,subQ48,subQ47,subQ0,subQ46,subQ45,subQ44,subQ43,subQ42,subQ41,subQ40,subQ39,subQ38,subQ37,subQ36,subQ35,subQ34,subQ33,subQ32,subQ31,subQ30,subQ29,subQ28,subQ27,subQ26,subQ25,subQ24,subQ23,subQ22,subQ21,subQ20,subQ19,subQ18,subQ17,subQ16,subQ15,subQ14])],"isStart":true}),subQ51,subQ1,subQ54,subQ50,subQ63])],"derivedFrom":subQ62}),makeQuery(id+"F20.boolean.opBoolean","SPLIT",FACE,{"disambiguationData":[TD([subQ5,subQ52,subQ53,subQ3,makeQuery(id+"F13.opFillet","BLEND_FACE",FACE,{"disambiguationData":[OSD([subQ10,subQ4,subQ2,subQ8])]}),makeQuery(id+"F15.opFillet","BLEND_FACE",FACE,{"disambiguationData":[OSD([subQ10,subQ4]),TDD([subQ13]),OD(1.0)]}),makeQuery(id+"F15.opFillet","BLEND_FACE",FACE,{"disambiguationData":[OSD([subQ10,subQ4]),TDD([subQ13]),OD(2.0)]}),makeQuery(id+"F17.opRevolve","CAP_FACE",FACE,{"disambiguationData":[OSD([subQ49,subQ48,subQ47,subQ0,subQ46,subQ45,subQ44,subQ43,subQ42,subQ41,subQ40,subQ39,subQ38,subQ37,subQ36,subQ35,subQ34,subQ33,subQ32,subQ31,subQ30,subQ29,subQ28,subQ27,subQ26,subQ25,subQ24,subQ23,subQ22,subQ21,subQ20,subQ19,subQ18,subQ17,subQ16,subQ15,subQ14])],"isStart":false}),subQ51,subQ1,subQ54,subQ55,subQ50])],"derivedFrom":subQ62})]})});}
            var sketch = newSketch(context, id + "F26", { "sketchPlane" : qUnion([Q0])});
            skCircle(sketch, "E112", {"center": v(-17.66, 29) * mm, "radius": 3 * mm});
            skCircle(sketch, "E113", {"center": v(-17.66, -29) * mm, "radius": 3 * mm});
            skCircle(sketch, "E114", {"center": v(-75.64, 29) * mm, "radius": 3 * mm});
            skCircle(sketch, "E115", {"center": v(-75.64, -29) * mm, "radius": 3 * mm});
            skSolve(sketch);
        }
        {
            var Q0;
            Q0=makeQuery(id+"F26.imprint","IMPRINT",FACE,{"disambiguationData":[TD([[makeQuery(id+"F26.imprint","IMPRINT",EDGE,{"derivedFrom":sQuery(id+"F26.wireOp",EDGE,"E114")}),1.0]])]});
            var Q1;
            Q1=makeQuery(id+"F26.imprint","IMPRINT",FACE,{"disambiguationData":[TD([[makeQuery(id+"F26.imprint","IMPRINT",EDGE,{"derivedFrom":sQuery(id+"F26.wireOp",EDGE,"E115")}),1.0]])]});
            extrude(context, id + "F27", {"entities" : qUnion([Q0, Q1]), "operationType" : NewBodyOperationType.REMOVE, "oppositeDirection" : true, "depth" : 25 * mm, "offsetDistance" : 25 * mm});
        }
        {
            var Q0;
            Q0=makeQuery(id+"F7.opExtrude","SWEPT_FACE",FACE,{"disambiguationData":[OSD([sQuery(id+"F6.wireOp",EDGE,"E56")])]});
            var sketch = newSketch(context, id + "F28", { "sketchPlane" : qUnion([Q0])});
            skCircle(sketch, "E116", {"center": v(-48.93, -13.44) * mm, "radius": 2.5 * mm});
            skCircle(sketch, "E117", {"center": v(-48.94, 13.43) * mm, "radius": 2.5 * mm});
            skCircle(sketch, "E118", {"center": v(-22.07, 13.44) * mm, "radius": 2.5 * mm});
            skCircle(sketch, "E119", {"center": v(-22.07, -13.44) * mm, "radius": 2.5 * mm});
            skSolve(sketch);
        }
        {
            var Q0;
            Q0 = qSketchRegion(id + "F28", true);
            extrude(context, id + "F29", {"entities" : qUnion([Q0]), "operationType" : NewBodyOperationType.REMOVE, "oppositeDirection" : true, "depth" : 250 * mm, "offsetDistance" : 25 * mm});
        }
    });
